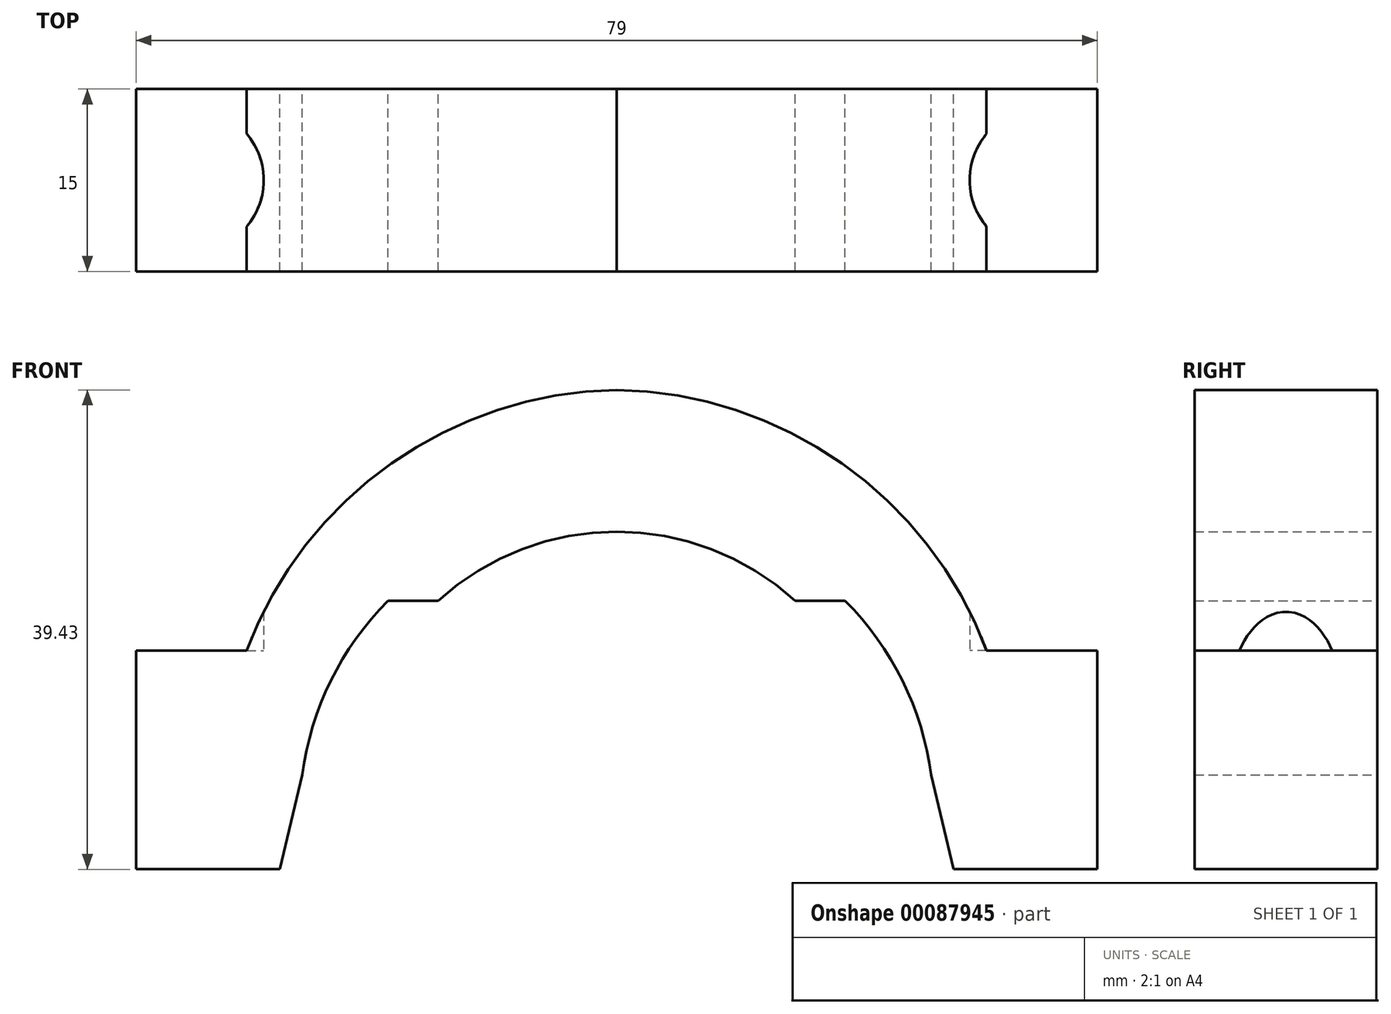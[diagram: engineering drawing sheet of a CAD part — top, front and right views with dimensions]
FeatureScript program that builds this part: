
annotation { "Feature Type Name" : "Feature", "Feature Type Description" : "" }
export const myFeature = defineFeature(function(context is Context, id is Id, definition is map)
    precondition{}
    {
        {
            var Q0;
            Q0=qCreatedBy(makeId("Front.planeOp"),FACE);
            var sketch = newSketch(context, id + "F0", { "sketchPlane" : qUnion([Q0])});
            skLineSegment(sketch, "E0", {"start": v(20.08, 0.25) * mm, "end": v(24.18, 0.25) * mm});
            skArc(sketch, "E1", {"start": v(20.08, 0.25) * mm, "mid": v(5.4, 5.92) * mm, "end": v(-9.28, 0.25) * mm});
            skArc(sketch, "E2", {"start": v(31.23, -14.07) * mm, "mid": v(28.9, -6.33) * mm, "end": v(24.18, 0.25) * mm});
            skLineSegment(sketch, "E3", {"start": v(31.23, -14.07) * mm, "end": v(33.1, -21.84) * mm});
            skLineSegment(sketch, "E4", {"start": v(5.4, 5.92) * mm, "end": v(5.4, -15.9) * mm, "construction": true});
            skLineSegment(sketch, "E5.MirrorCS", {"start": v(-9.28, 0.25) * mm, "end": v(-13.38, 0.25) * mm});
            skLineSegment(sketch, "E6.MirrorCS", {"start": v(-20.43, -14.07) * mm, "end": v(-22.3, -21.84) * mm});
            skArc(sketch, "E7.MirrorCS", {"start": v(-20.43, -14.07) * mm, "mid": v(-18.1, -6.33) * mm, "end": v(-13.38, 0.25) * mm});
            skLineSegment(sketch, "E8", {"start": v(33.1, -21.84) * mm, "end": v(44.9, -21.84) * mm});
            skLineSegment(sketch, "E9", {"start": v(44.9, -21.84) * mm, "end": v(44.9, -3.84) * mm});
            skLineSegment(sketch, "E10", {"start": v(44.9, -3.84) * mm, "end": v(35.8, -3.84) * mm});
            skArc(sketch, "E11", {"start": v(35.8, -3.84) * mm, "mid": v(23.9, 11.56) * mm, "end": v(5.4, 17.59) * mm});
            skLineSegment(sketch, "E12.MirrorCS", {"start": v(-22.3, -21.84) * mm, "end": v(-34.1, -21.84) * mm});
            skLineSegment(sketch, "E13.MirrorCS", {"start": v(-34.1, -3.84) * mm, "end": v(-25, -3.84) * mm});
            skLineSegment(sketch, "E14.MirrorCS", {"start": v(-34.1, -21.84) * mm, "end": v(-34.1, -3.84) * mm});
            skArc(sketch, "E15.MirrorCS", {"start": v(-25, -3.84) * mm, "mid": v(-13.1, 11.56) * mm, "end": v(5.4, 17.59) * mm});
            skSolve(sketch);
        }
        {
            var Q0;
            Q0 = qSketchRegion(id + "F0", true);
            extrude(context, id + "F1", {"entities" : qUnion([Q0]), "depth" : 15 * mm});
        }
        {
            var Q0;
            Q0=makeQuery(id+"F1.opExtrude","SWEPT_FACE",FACE,{"disambiguationData":[OSD([sQuery(id+"F0.wireOp",EDGE,"E13.MirrorCS")])]});
            var sketch = newSketch(context, id + "F2", { "sketchPlane" : qUnion([Q0])});
            skLineSegment(sketch, "E16", {"start": v(-29.55, 0) * mm, "end": v(-29.55, -15) * mm, "construction": true});
            skCircle(sketch, "E17", {"center": v(-29.55, -7.5) * mm, "radius": 2.38 * mm});
            skCircle(sketch, "E18.MirrorC", {"center": v(40.35, -7.5) * mm, "radius": 2.38 * mm});
            skCircle(sketch, "E19", {"center": v(-29.55, -7.5) * mm, "radius": 5.94 * mm});
            skCircle(sketch, "E20.MirrorC", {"center": v(40.35, -7.5) * mm, "radius": 5.94 * mm});
            skSolve(sketch);
        }
        {
            var Q0;
            Q0 = qSketchRegion(id + "F2", true);
            extrude(context, id + "F3", {"entities" : qUnion([Q0]), "operationType" : NewBodyOperationType.REMOVE, "depth" : 25.4 * mm});
        }
    });
